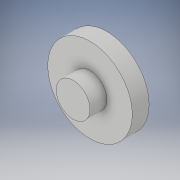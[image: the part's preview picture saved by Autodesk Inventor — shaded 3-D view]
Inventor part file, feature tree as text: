
AUTODESK INVENTOR PART (.ipt)
format: ipt  version: 2019 (Build 230136000, 136)  size: 104,448 bytes
history: native  units: mm
features: extrude x2, sketch x2, other x1
ambient origin geometry x8: Origin, YZ Plane, XZ Plane, XY Plane, X Axis, Y Axis, Z Axis, Center Point
bodies: Body1 (feature_tree)
feature tree (5):
  other  "Твердое тело1"
  extrude  "Выдавливание1"  Depth=50.0mm
  extrude  "Выдавливание2"  Depth=10.0mm TaperAngle=0.0deg
  sketch  "Эскиз1"
  sketch  "Эскиз2"
